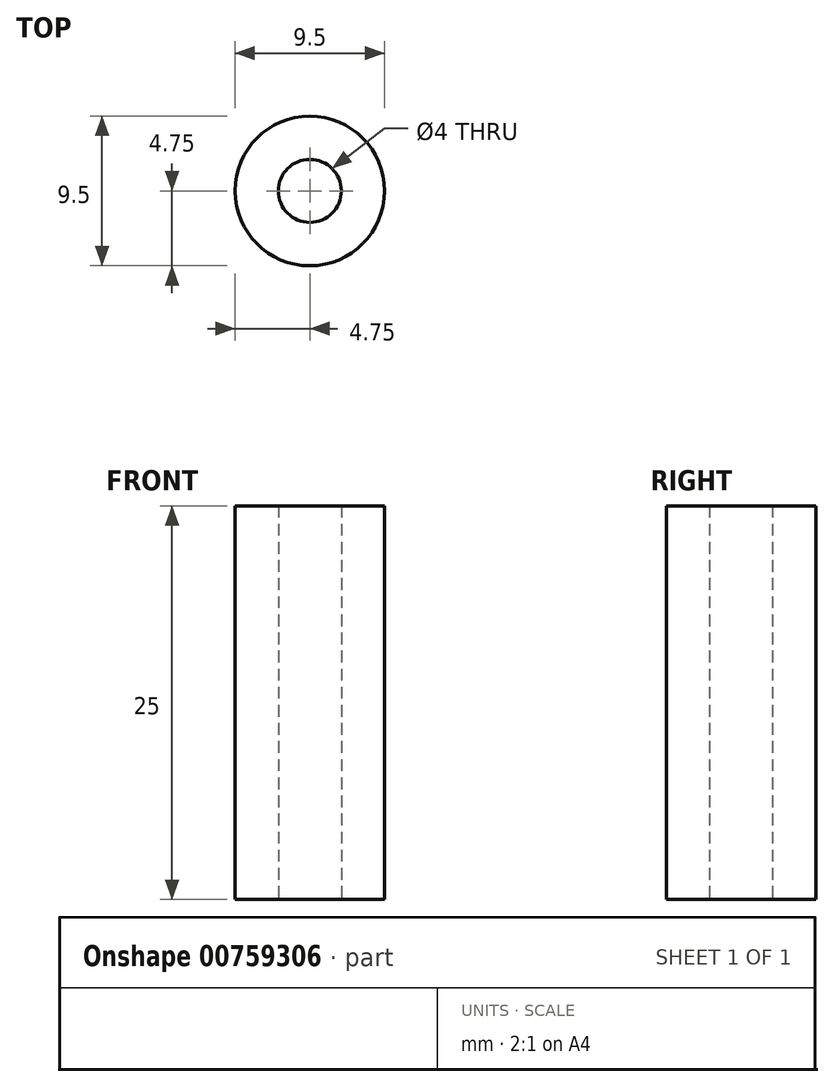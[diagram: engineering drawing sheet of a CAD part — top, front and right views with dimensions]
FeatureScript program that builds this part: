
annotation { "Feature Type Name" : "Feature", "Feature Type Description" : "" }
export const myFeature = defineFeature(function(context is Context, id is Id, definition is map)
    precondition{}
    {
        {
            var Q0;
            Q0=qCreatedBy(makeId("Top.planeOp"),FACE);
            var sketch = newSketch(context, id + "F0", { "sketchPlane" : qUnion([Q0])});
            skCircle(sketch, "E0", {"center": v(0, 0) * mm, "radius": 4.75 * mm});
            skCircle(sketch, "E1", {"center": v(0, 0) * mm, "radius": 2 * mm});
            skSolve(sketch);
        }
        {
            var Q0;
            Q0=makeQuery(id+"F0.imprint","IMPRINT",FACE,{"disambiguationData":[TD([[makeQuery(id+"F0.imprint","IMPRINT",EDGE,{"derivedFrom":sQuery(id+"F0.wireOp",EDGE,"E0")}),1.0]])]});
            extrude(context, id + "F1", {"entities" : qUnion([Q0]), "depth" : 25 * mm, "offsetDistance" : 25 * mm});
        }
    });
